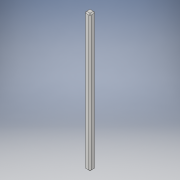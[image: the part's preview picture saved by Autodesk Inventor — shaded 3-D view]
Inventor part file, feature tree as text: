
AUTODESK INVENTOR PART (.ipt)
format: ipt  version: 2019 (Build 230136000, 136)  size: 108,544 bytes
history: native  units: in
note: dims shown in document units (in); Inventor stores cm internally (conversion verified against a paired STEP export)
features: extrude x1, chamfer x1, sketch x1
ambient origin geometry x8: Origin, YZ Plane, XZ Plane, XY Plane, X Axis, Y Axis, Z Axis, Center Point
bodies: Solid1 (feature_tree)
feature tree (3):
  extrude  "Extrusion1"  Depth=23.622in
  chamfer  "Chamfer1"  Distance=0.9843in
  sketch  "Sketch1"  dims[d0=0.9843in d1=23.622in d2=0.9843in d3=0.0in d4=0.1969in d5=0.0787in d6=45.0deg]
